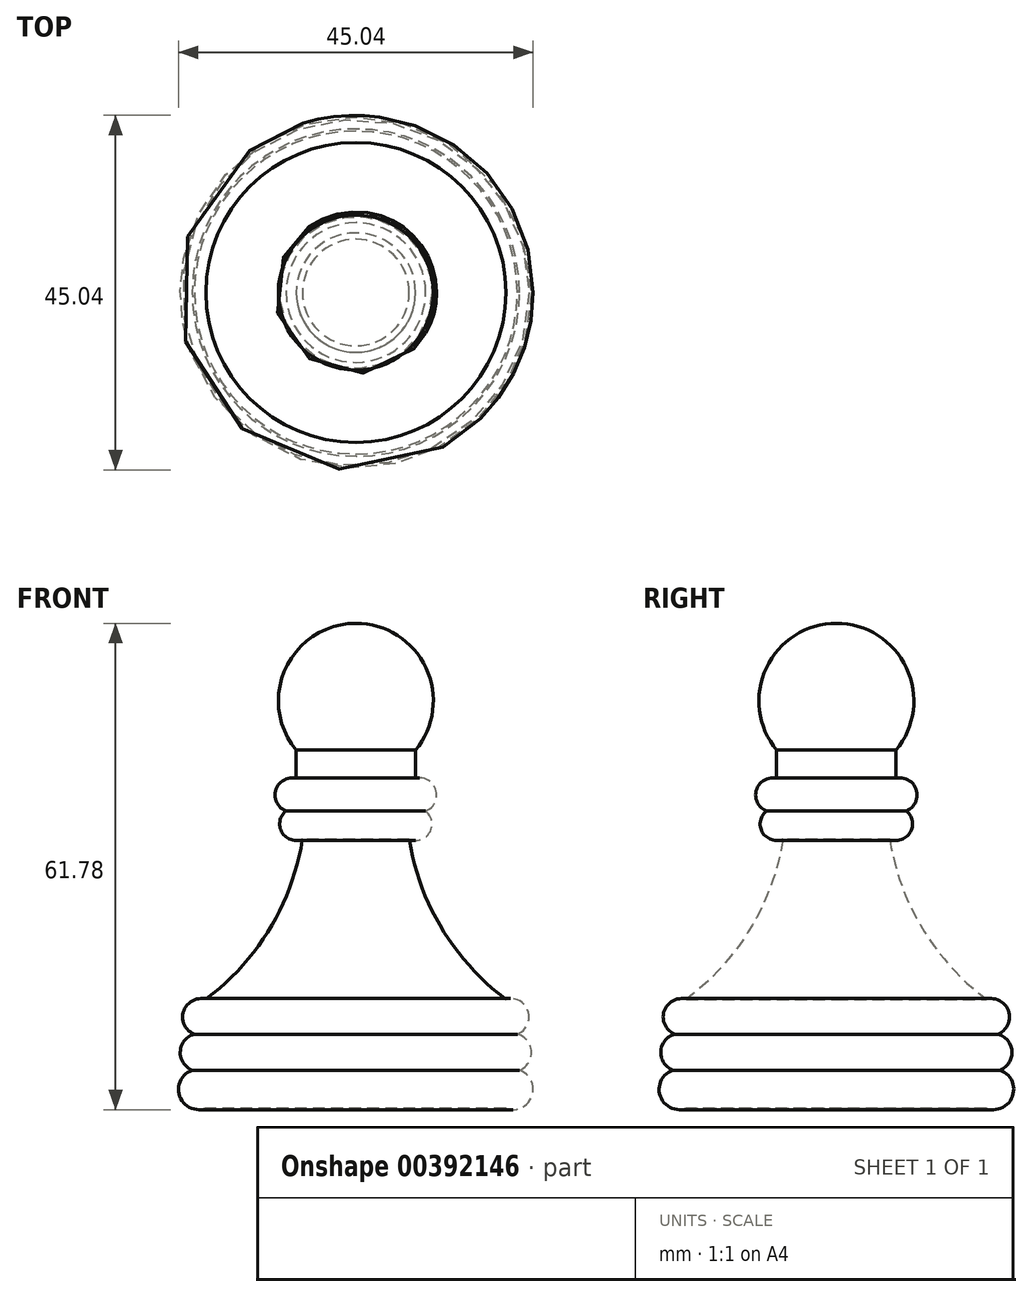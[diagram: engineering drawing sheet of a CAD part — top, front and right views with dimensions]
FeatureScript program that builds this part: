
annotation { "Feature Type Name" : "Feature", "Feature Type Description" : "" }
export const myFeature = defineFeature(function(context is Context, id is Id, definition is map)
    precondition{}
    {
        {
            var Q0;
            Q0=qCreatedBy(makeId("Front.planeOp"),FACE);
            var sketch = newSketch(context, id + "F0", { "sketchPlane" : qUnion([Q0])});
            skLineSegment(sketch, "E0", {"start": v(0, 12.73) * mm, "end": v(0, -38.07) * mm});
            skLineSegment(sketch, "E1", {"start": v(0, -38.07) * mm, "end": v(-19.05, -38.07) * mm});
            skArc(sketch, "E2", {"start": v(-19.05, -33.23) * mm, "mid": v(-22.52, -35.65) * mm, "end": v(-19.05, -38.07) * mm});
            skArc(sketch, "E3", {"start": v(-19.05, -28.71) * mm, "mid": v(-22.31, -30.97) * mm, "end": v(-19.05, -33.23) * mm});
            skArc(sketch, "E4", {"start": v(-19.05, -24.2) * mm, "mid": v(-22, -26.45) * mm, "end": v(-19.05, -28.71) * mm});
            skArc(sketch, "E5", {"start": v(-19.05, -24.2) * mm, "mid": v(-10.93, -15.23) * mm, "end": v(-6.78, -3.87) * mm});
            skArc(sketch, "E6", {"start": v(-6.78, 0) * mm, "mid": v(-9.68, -1.94) * mm, "end": v(-6.78, -3.87) * mm});
            skArc(sketch, "E7", {"start": v(-7.58, 3.87) * mm, "mid": v(-10.21, 1.3) * mm, "end": v(-6.78, 0) * mm});
            skArc(sketch, "E8", {"start": v(0, 23.55) * mm, "mid": v(-8.9, 17.9) * mm, "end": v(-7.58, 7.44) * mm});
            skLineSegment(sketch, "E9", {"start": v(0, 12.73) * mm, "end": v(0, 23.55) * mm});
            skLineSegment(sketch, "E10", {"start": v(-7.58, 3.87) * mm, "end": v(-7.58, 7.44) * mm});
            skPoint(sketch, "E11.orphan", {"position": v(0, 3.87) * mm});
            skSolve(sketch);
        }
        {
            var Q0;
            Q0 = qSketchRegion(id + "F0", true);
            var Q1;
            Q1=sQuery(id+"F0.wireOp",EDGE,"E0");
            revolve(context, id + "F1", {"entities" : qUnion([Q0]), "axis" : qUnion([Q1]), "revolveType" : RevolveType.FULL});
        }
        {
            var Q0;
            Q0 = qSketchRegion(id + "F0", true);
            var Q1;
            Q1=sQuery(id+"F0.wireOp",EDGE,"E0");
            revolve(context, id + "F2", {"entities" : qUnion([Q0]), "axis" : qUnion([Q1]), "revolveType" : RevolveType.FULL});
        }
    });
